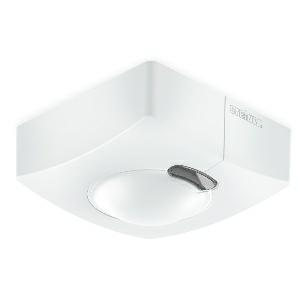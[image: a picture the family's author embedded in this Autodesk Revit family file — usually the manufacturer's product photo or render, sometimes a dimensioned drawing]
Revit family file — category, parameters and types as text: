
# Revit family: hf_3360_011604
name_source: partatom
category: Elektroinstallationen
revit_build: Autodesk Revit 2016 (Build: 20190508_0715(x64)
units: mm (PartAtom-declared; Revit-internal decimal feet)

## family parameters
Basisbauteil = Fläche
Beim Laden mit Abzugskörper schneiden = Nein
Bemaßung runder Anschluss = Durchmesser verwenden
Beschriftungsausrichtung beibehalten = Nein
Gemeinsam genutzt = Nein
Raumberechnungspunkt = Nein
Teiletyp = Normal

## types (1)
- HF 3360
    Apparent Load = 0 VA
    Beschreibung = Type: Motion detectors; Dimensions (L x W x H): 52 x 95 x 95 mm; Mains power supply: 220 – 240 V / 50 – 60 Hz; Sensor Technology: High frequency; Application, place: Indoors; Application, room: function room / ancillary room, stairwell, WC / washroom, multi-storey / underground car park, Indoors; Installation site: wall, ceiling, corner; Installation: Surface wiring; HF-system: 5,8 GHz; Electronic scalability: Yes; Mechanical scalability: No; Mounting height: 2,00 – 4,00 m; Optimum mounting height: 2,8 m; Detection: also through glass, wood and stud walls; Detection angle: 360 °; Angle of aperture: 140 °; Sneak-by guard: Yes; Reach, radial: Ø 8 m (50 m²); Reach, tangential: Ø 8 m (50 m²); Twilight setting TEACH: Yes; Twilight setting: 2 – 1000 lx; Time setting: 5 sec – 15 min; Control output, Dali: Broadcast 1x30 electronic ballasts; Constant-lighting control: Yes; Basic light level function: Yes; Basic light level function in per cent: 10 – 50 %; Basic light level function time: 1-30 min, all night; Basic light level function percentage, from: 10 %; Basic light level function percentage, up to: 50 %; Functions: Normal / test mode, Manual ON / ON-OFF, Constant-lighting control ON-OFF; Settings via: Remote control, Potentiometers, Smart Remote; With remote control: No; Interconnection: Yes; IP-rating: IP54; Material: Plastic; Ambient temperature: -20 – 50 °C; Colour: white; Colour, RAL: 9003; Manufacturer's Warranty: 5 years; Version: DALI-2 Application Controller - surface, sq.; PU1, EAN: 4007841011604
    Height = 95 mm
    Hersteller = Steinel
    Length = 52 mm  [stored 0.170604 ft]
    ModVariant = Nein
    Modell = 011604
    Mounting Type = Surface mounted
    Number of Poles = 1
    OnlyDefault = Ja
    Power Factor = 1
    Product Name = HF 3360
    Product group = Sensor-switched indoor light
    ProductGroupID = 30
    Protection Class = Protection class
    Protection Degree = IP 54
    RlxData = <blob elided: 26217 chars, md5=f7df9932>
    SensorDataFile = {"IESDataFiles":[]}
    Typenbild = produkt1_011604.jpg
    Typenkommentare = Product without accessories
    URL = http://relux.com
    VarID = ---
    Voltage = 0 V
    Vorgabe-Ansicht = 1800 mm
    Weight = 0.00 kg
    Width = 95 mm

note: [stored X ft] marks values corroborated as IEEE doubles in the binary element streams (Revit-internal decimal feet)

## geometry (parser evidence)
native form markers: Blend x4, Sweep x10
no freeform markers — native parametric forms only
